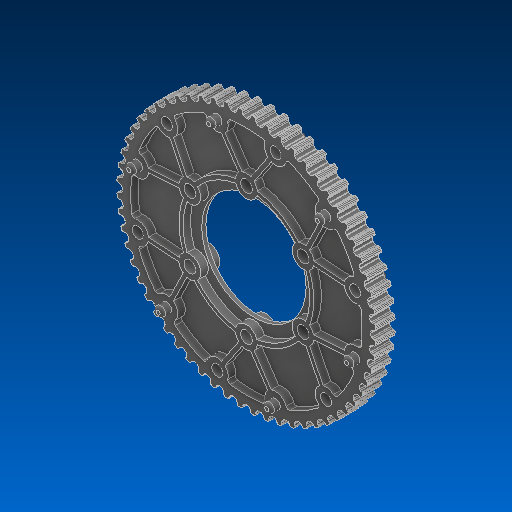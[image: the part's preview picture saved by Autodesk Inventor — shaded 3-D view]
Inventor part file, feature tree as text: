
AUTODESK INVENTOR PART (.ipt)
format: ipt  version: 2022.2 (Build 262287000, 287)  size: 1,637,888 bytes
history: native  units: in
note: dims shown in document units (in); Inventor stores cm internally (conversion verified against a paired STEP export)
features: fillet x1
ambient origin geometry x8: Origin, YZ Plane, XZ Plane, XY Plane, X Axis, Y Axis, Z Axis, Center Point
bodies: Solid1 (feature_tree)
feature tree (1):
  fillet  "Fillet3"  [1 undecoded]
note: 1 required parameter value undecoded (feature->parameter linkage not recoverable at this tier; creation-order binding heuristic only, values carry confidence <= 0.55)
